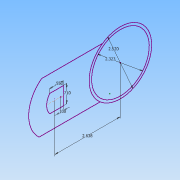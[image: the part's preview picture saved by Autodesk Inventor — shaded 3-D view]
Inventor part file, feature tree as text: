
AUTODESK INVENTOR PART (.ipt)
format: ipt  version: 2015 (Build 190159000, 159)  size: 71,168 bytes
history: native  units: in
note: dims shown in document units (in); Inventor stores cm internally (conversion verified against a paired STEP export)
features: sketch x1
ambient origin geometry x8: Origin, YZ Plane, XZ Plane, XY Plane, X Axis, Y Axis, Z Axis, Center Point
feature tree (1):
  sketch  "Sketch1"  dims[d0=0.71in d1=0.55in d2=0.1in d3=2.3228in d4=2.5197in d6=2.6378in]
